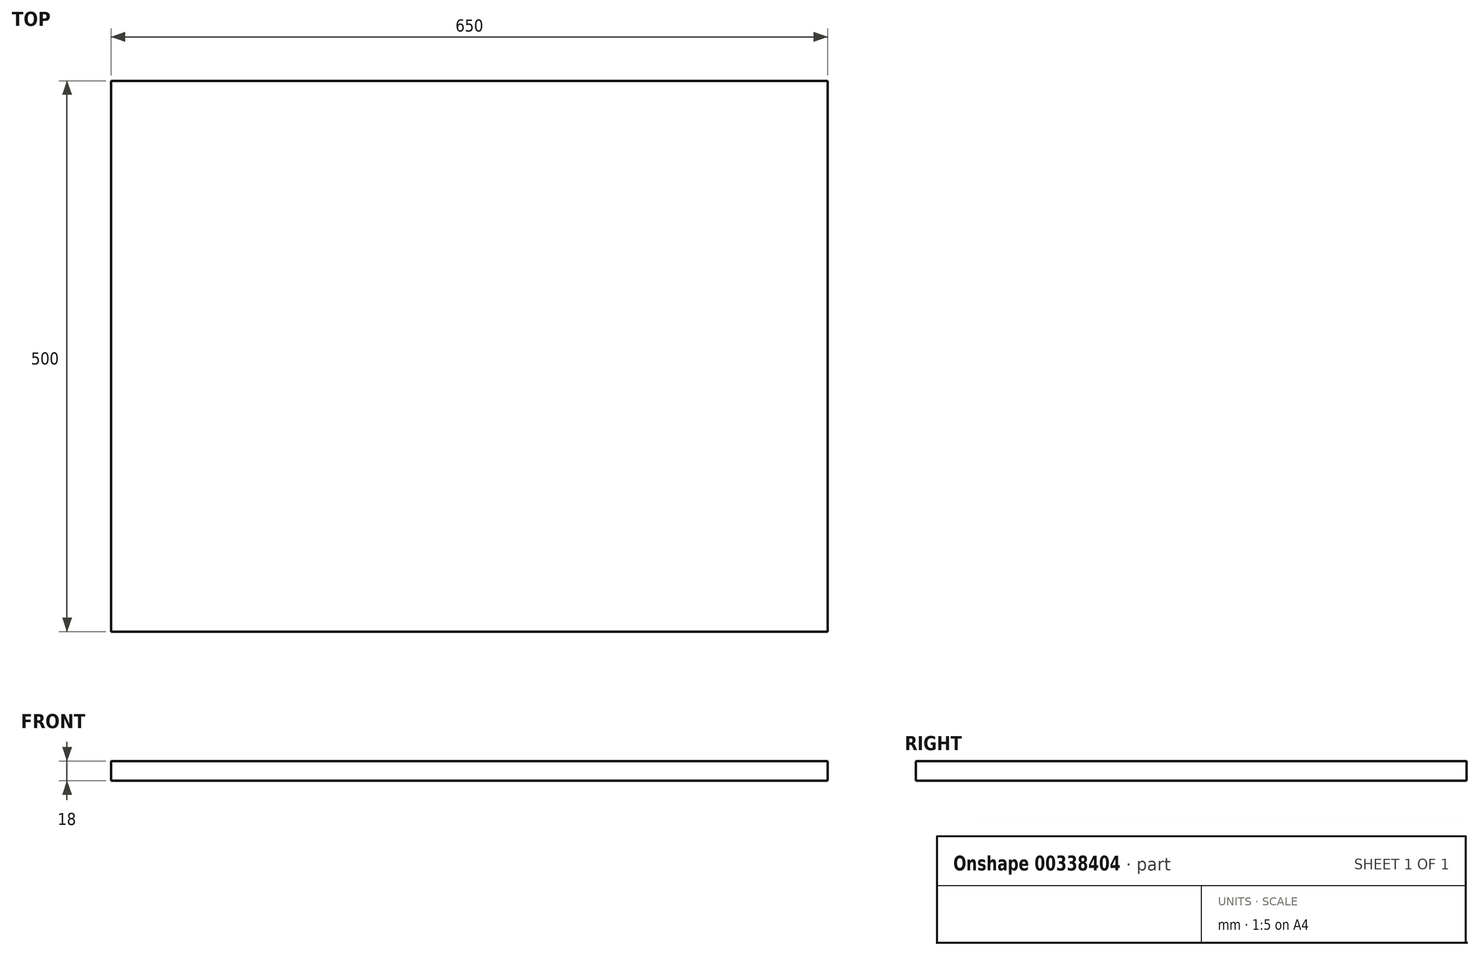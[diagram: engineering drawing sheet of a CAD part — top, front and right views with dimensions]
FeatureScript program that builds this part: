
annotation { "Feature Type Name" : "Feature", "Feature Type Description" : "" }
export const myFeature = defineFeature(function(context is Context, id is Id, definition is map)
    precondition{}
    {
        {
            var Q0;
            Q0=qCreatedBy(makeId("Top.planeOp"),FACE);
            var sketch = newSketch(context, id + "F0", { "sketchPlane" : qUnion([Q0])});
            skLineSegment(sketch, "E0.bottom", {"start": v(-325, -250) * mm, "end": v(325, -250) * mm});
            skLineSegment(sketch, "E0.top", {"start": v(-325, 250) * mm, "end": v(325, 250) * mm});
            skLineSegment(sketch, "E0.left", {"start": v(-325, -250) * mm, "end": v(-325, 250) * mm});
            skLineSegment(sketch, "E0.right", {"start": v(325, -250) * mm, "end": v(325, 250) * mm});
            skPoint(sketch, "E0.middle", {"position": v(0, 0) * mm});
            skSolve(sketch);
        }
        {
            var Q0;
            Q0=makeQuery(id+"F0.imprint","IMPRINT",FACE,{"disambiguationData":[TD([[makeQuery(id+"F0.imprint","IMPRINT",EDGE,{"derivedFrom":sQuery(id+"F0.wireOp",EDGE,"E0.bottom")}),1.0]])]});
            extrude(context, id + "F1", {"entities" : qUnion([Q0]), "offsetDistance" : 25 * mm, "depth" : 18 * mm});
        }
    });
